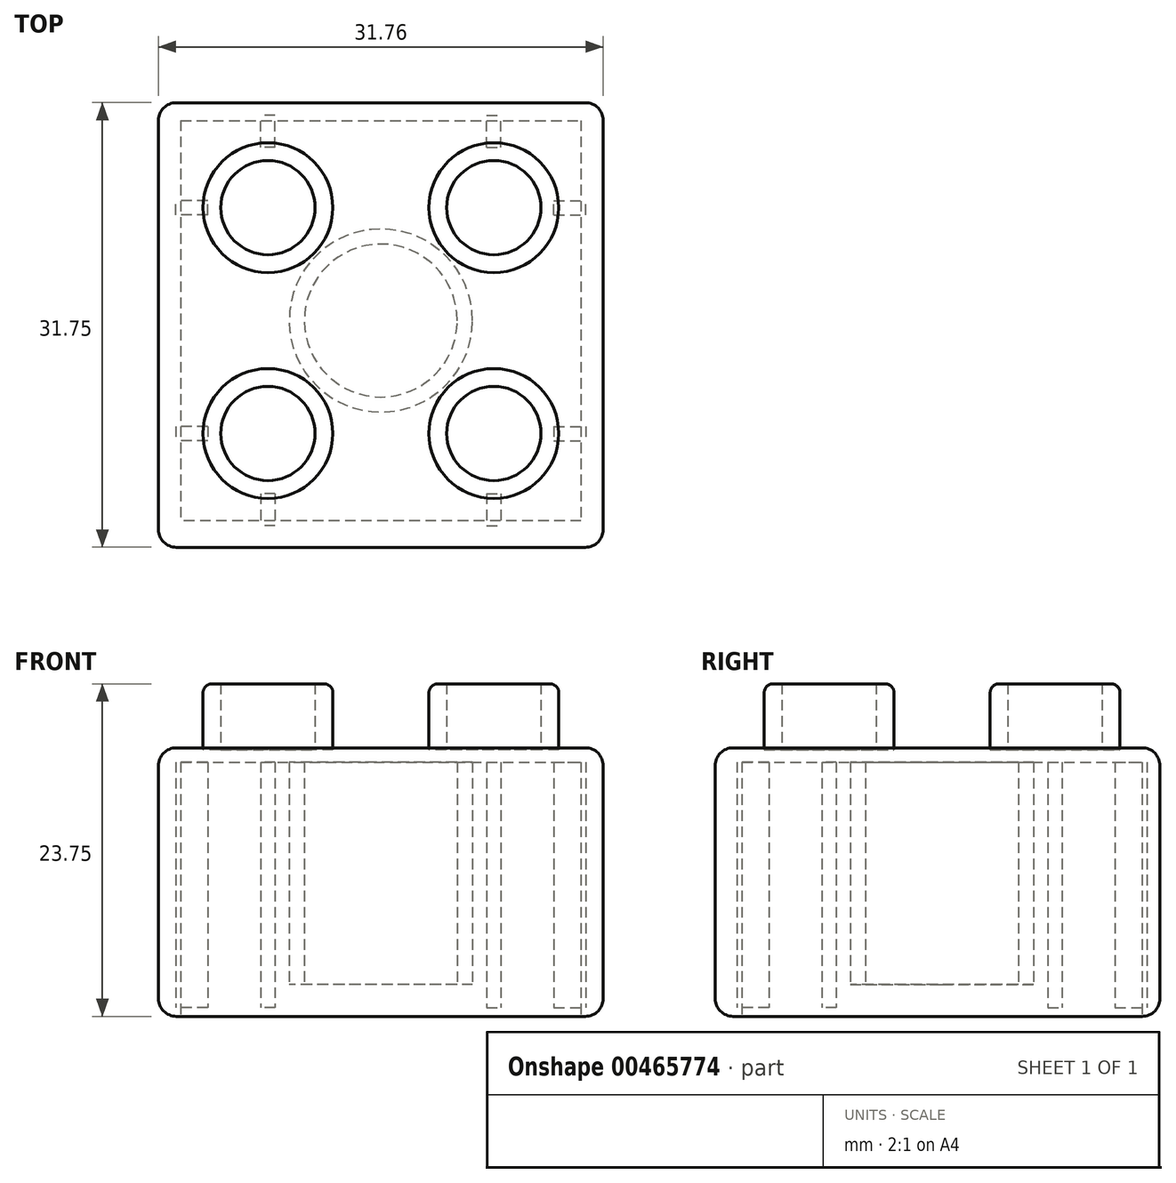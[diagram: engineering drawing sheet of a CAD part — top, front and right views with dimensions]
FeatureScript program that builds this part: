
annotation { "Feature Type Name" : "Feature", "Feature Type Description" : "" }
export const myFeature = defineFeature(function(context is Context, id is Id, definition is map)
    precondition{}
    {
        {
            var Q0;
            Q0=qCreatedBy(makeId("Top.planeOp"),FACE);
            var sketch = newSketch(context, id + "F0", { "sketchPlane" : qUnion([Q0])});
            skPoint(sketch, "E0", {"position": v(0, 16.87) * mm});
            skPoint(sketch, "E1", {"position": v(0, 15.88) * mm});
            skPoint(sketch, "E2", {"position": v(0, -14.88) * mm});
            skPoint(sketch, "E3", {"position": v(0, -15.88) * mm});
            skPoint(sketch, "E4", {"position": v(17.1, 0) * mm});
            skPoint(sketch, "E5", {"position": v(15.88, 0) * mm});
            skPoint(sketch, "E6", {"position": v(-15.88, 0) * mm});
            skPoint(sketch, "E7", {"position": v(15.64, 15.88) * mm});
            skPoint(sketch, "E8", {"position": v(15.88, 15.56) * mm});
            skPoint(sketch, "E9", {"position": v(-16.3, -15.88) * mm});
            skPoint(sketch, "E10", {"position": v(-15.88, -16.2) * mm});
            skLineSegment(sketch, "E11.bottom", {"start": v(-15.88, -16.2) * mm, "end": v(15.88, -16.2) * mm});
            skLineSegment(sketch, "E11.top", {"start": v(-15.88, 15.56) * mm, "end": v(15.88, 15.56) * mm});
            skLineSegment(sketch, "E11.left", {"start": v(-15.88, -16.2) * mm, "end": v(-15.88, 15.56) * mm});
            skLineSegment(sketch, "E11.right", {"start": v(15.88, -16.2) * mm, "end": v(15.88, 15.56) * mm});
            skSolve(sketch);
        }
        {
            var Q0;
            Q0=makeQuery(id+"F0.imprint","IMPRINT",FACE,{"disambiguationData":[TD([[makeQuery(id+"F0.imprint","IMPRINT",EDGE,{"derivedFrom":sQuery(id+"F0.wireOp",EDGE,"E11.bottom")}),1.0]])]});
            var sketch = newSketch(context, id + "F1", { "sketchPlane" : qUnion([Q0])});
            skPoint(sketch, "E12", {"position": v(14.77, 0) * mm});
            skPoint(sketch, "E13", {"position": v(14.29, 0) * mm});
            skPoint(sketch, "E14", {"position": v(-14.29, 0) * mm});
            skPoint(sketch, "E15", {"position": v(-14.29, -14.92) * mm});
            skPoint(sketch, "E16", {"position": v(-14.29, -14.29) * mm});
            skPoint(sketch, "E17", {"position": v(14.29, 14.33) * mm});
            skPoint(sketch, "E18", {"position": v(14.29, 14.29) * mm});
            skLineSegment(sketch, "E19.bottom", {"start": v(-14.29, -14.29) * mm, "end": v(14.29, -14.29) * mm});
            skLineSegment(sketch, "E19.top", {"start": v(-14.29, 14.29) * mm, "end": v(14.29, 14.29) * mm});
            skLineSegment(sketch, "E19.left", {"start": v(-14.29, -14.29) * mm, "end": v(-14.29, 14.29) * mm});
            skLineSegment(sketch, "E19.right", {"start": v(14.29, -14.29) * mm, "end": v(14.29, 14.29) * mm});
            skSolve(sketch);
        }
        {
            var Q0;
            Q0=makeQuery(id+"F1.imprint","IMPRINT",FACE,{"disambiguationData":[TD([[makeQuery(id+"F1.imprint","IMPRINT",EDGE,{"derivedFrom":sQuery(id+"F1.wireOp",EDGE,"E19.bottom")}),1.0]])]});
            var sketch = newSketch(context, id + "F2", { "sketchPlane" : qUnion([Q0])});
            skPoint(sketch, "E20", {"position": v(0, 0) * mm});
            skCircle(sketch, "E21", {"center": v(0, 0) * mm, "radius": 6.54 * mm});
            skSolve(sketch);
        }
        {
            var Q0;
            Q0=makeQuery(id+"F1.imprint","IMPRINT",FACE,{"disambiguationData":[TD([[makeQuery(id+"F1.imprint","IMPRINT",EDGE,{"derivedFrom":sQuery(id+"F1.wireOp",EDGE,"E19.bottom")}),1.0]])]});
            var sketch = newSketch(context, id + "F3", { "sketchPlane" : qUnion([Q0])});
            skPoint(sketch, "E22", {"position": v(0, 0) * mm});
            skCircle(sketch, "E23", {"center": v(0, 0) * mm, "radius": 5.46 * mm});
            skSolve(sketch);
        }
        {
            var Q0;
            Q0=makeQuery(id+"F1.imprint","IMPRINT",FACE,{"disambiguationData":[TD([[makeQuery(id+"F1.imprint","IMPRINT",EDGE,{"derivedFrom":sQuery(id+"F1.wireOp",EDGE,"E19.bottom")}),1.0]])]});
            var sketch = newSketch(context, id + "F4", { "sketchPlane" : qUnion([Q0])});
            skPoint(sketch, "E24", {"position": v(0, 1.02) * mm});
            skPoint(sketch, "E25", {"position": v(0, 0.95) * mm});
            skPoint(sketch, "E26", {"position": v(0, -0.95) * mm});
            skPoint(sketch, "E27", {"position": v(-0.23, 0) * mm});
            skPoint(sketch, "E28", {"position": v(-0.5, 0) * mm});
            skPoint(sketch, "E29", {"position": v(0.3, 0) * mm});
            skPoint(sketch, "E30", {"position": v(0.5, 0) * mm});
            skPoint(sketch, "E31", {"position": v(-0.5, -0.86) * mm});
            skPoint(sketch, "E32", {"position": v(-0.5, -1.5) * mm});
            skPoint(sketch, "E33", {"position": v(0.5, 0.79) * mm});
            skLineSegment(sketch, "E34.bottom", {"start": v(-0.5, -1.5) * mm, "end": v(0.5, -1.5) * mm});
            skLineSegment(sketch, "E34.top", {"start": v(-0.5, 0.79) * mm, "end": v(0.5, 0.79) * mm});
            skLineSegment(sketch, "E34.left", {"start": v(-0.5, -1.5) * mm, "end": v(-0.5, 0.79) * mm});
            skLineSegment(sketch, "E34.right", {"start": v(0.5, -1.5) * mm, "end": v(0.5, 0.79) * mm});
            skPoint(sketch, "E35", {"position": v(14.29, -8.12) * mm});
            skPoint(sketch, "E36", {"position": v(12.29, -8.12) * mm});
            skSolve(sketch);
        }
        {
            var Q0;
            Q0=qSketchRegion(id+"F0",true);
            extrude(context, id + "F5", {"entities" : qUnion([Q0]), "depth" : 19.18 * mm});
        }
        {
            var Q0;
            Q0=qSketchRegion(id+"F1",true);
            extrude(context, id + "F6", {"entities" : qUnion([Q0]), "operationType" : NewBodyOperationType.REMOVE, "depth" : 18.16 * mm, "hasSecondDirection" : true, "secondDirectionOppositeDirection" : true, "secondDirectionDepth" : 0.38 * mm});
        }
        {
            var Q0;
            Q0=qSketchRegion(id+"F2",true);
            extrude(context, id + "F7", {"entities" : qUnion([Q0]), "operationType" : NewBodyOperationType.ADD, "depth" : 15.88 * mm});
        }
        {
            var Q0;
            Q0=qSketchRegion(id+"F3",true);
            extrude(context, id + "F8", {"entities" : qUnion([Q0]), "operationType" : NewBodyOperationType.REMOVE, "depth" : 15.88 * mm, "hasSecondDirection" : true, "secondDirectionOppositeDirection" : true, "secondDirectionDepth" : 0.64 * mm});
        }
        {
            var Q0;
            Q0=makeQuery(id+"F7.opExtrude","SWEPT_BODY",BODY,{"disambiguationData":[OSD([sQuery(id+"F2.wireOp",EDGE,"E21")])]});
            transform(context, id + "F9", {"entities" : qUnion([Q0]), "transformType" : TransformType.TRANSLATION_3D, "dx" : 0 * mm, "dy" : 0 * mm, "dz" : 2.3 * mm, "makeCopy" : false});
        }
        {
            var Q0;
            Q0=makeQuery(id+"F4.imprint","IMPRINT",FACE,{"disambiguationData":[TD([[makeQuery(id+"F4.imprint","IMPRINT",EDGE,{"derivedFrom":sQuery(id+"F4.wireOp",EDGE,"E34.bottom")}),1.0]])]});
            extrude(context, id + "F10", {"entities" : qUnion([Q0]), "operationType" : NewBodyOperationType.ADD, "depth" : 17.53 * mm});
        }
        {
            var Q0;
            Q0=makeQuery(id+"F10.opExtrude","SWEPT_BODY",BODY,{"disambiguationData":[OSD([sQuery(id+"F4.wireOp",EDGE,"E34.bottom"),sQuery(id+"F4.wireOp",EDGE,"E34.top"),sQuery(id+"F4.wireOp",EDGE,"E34.left"),sQuery(id+"F4.wireOp",EDGE,"E34.right")])]});
            transform(context, id + "F11", {"entities" : qUnion([Q0]), "transformType" : TransformType.TRANSLATION_3D, "dx" : 8.06 * mm, "dy" : 13.86 * mm, "dz" : 0.64 * mm, "makeCopy" : false});
        }
        {
            var Q0;
            Q0=makeQuery(id+"F10.opExtrude","SWEPT_BODY",BODY,{"disambiguationData":[OSD([sQuery(id+"F4.wireOp",EDGE,"E34.bottom"),sQuery(id+"F4.wireOp",EDGE,"E34.top"),sQuery(id+"F4.wireOp",EDGE,"E34.left"),sQuery(id+"F4.wireOp",EDGE,"E34.right")])]});
            var Q1;
            Q1=qCreatedBy(makeId("Front.planeOp"),FACE);
            mirror(context, id + "F12", {"entities" : qUnion([Q0]), "mirrorPlane" : qUnion([Q1])});
        }
        {
            var Q0;
            Q0=makeQuery(id+"F12.opPattern","COPY",BODY,{"derivedFrom":makeQuery(id+"F10.opExtrude","SWEPT_BODY",BODY,{"disambiguationData":[OSD([sQuery(id+"F4.wireOp",EDGE,"E34.bottom"),sQuery(id+"F4.wireOp",EDGE,"E34.top"),sQuery(id+"F4.wireOp",EDGE,"E34.left"),sQuery(id+"F4.wireOp",EDGE,"E34.right")])]}),"instanceName":"1"});
            var Q1;
            Q1=makeQuery(id+"F10.opExtrude","SWEPT_BODY",BODY,{"disambiguationData":[OSD([sQuery(id+"F4.wireOp",EDGE,"E34.bottom"),sQuery(id+"F4.wireOp",EDGE,"E34.top"),sQuery(id+"F4.wireOp",EDGE,"E34.left"),sQuery(id+"F4.wireOp",EDGE,"E34.right")])]});
            var Q2;
            Q2=qCreatedBy(makeId("Right.planeOp"),FACE);
            mirror(context, id + "F13", {"entities" : qUnion([Q0, Q1]), "mirrorPlane" : qUnion([Q2])});
        }
        {
            var Q0;
            Q0=qCreatedBy(makeId("Front.planeOp"),FACE);
            var sketch = newSketch(context, id + "F14", { "sketchPlane" : qUnion([Q0])});
            skLineSegment(sketch, "E37", {"start": v(0, 40.9) * mm, "end": v(0, -32.36) * mm});
            skSolve(sketch);
        }
        {
            var Q0;
            Q0=makeQuery(id+"F12.opPattern","COPY",BODY,{"derivedFrom":makeQuery(id+"F10.opExtrude","SWEPT_BODY",BODY,{"disambiguationData":[OSD([sQuery(id+"F4.wireOp",EDGE,"E34.bottom"),sQuery(id+"F4.wireOp",EDGE,"E34.top"),sQuery(id+"F4.wireOp",EDGE,"E34.left"),sQuery(id+"F4.wireOp",EDGE,"E34.right")])]}),"instanceName":"1"});
            var Q1;
            Q1=makeQuery(id+"F13.opPattern","COPY",BODY,{"derivedFrom":makeQuery(id+"F12.opPattern","COPY",BODY,{"derivedFrom":makeQuery(id+"F10.opExtrude","SWEPT_BODY",BODY,{"disambiguationData":[OSD([sQuery(id+"F4.wireOp",EDGE,"E34.bottom"),sQuery(id+"F4.wireOp",EDGE,"E34.top"),sQuery(id+"F4.wireOp",EDGE,"E34.left"),sQuery(id+"F4.wireOp",EDGE,"E34.right")])]}),"instanceName":"1"}),"instanceName":"1"});
            var Q2;
            Q2=makeQuery(id+"F10.opExtrude","SWEPT_BODY",BODY,{"disambiguationData":[OSD([sQuery(id+"F4.wireOp",EDGE,"E34.bottom"),sQuery(id+"F4.wireOp",EDGE,"E34.top"),sQuery(id+"F4.wireOp",EDGE,"E34.left"),sQuery(id+"F4.wireOp",EDGE,"E34.right")])]});
            var Q3;
            Q3=makeQuery(id+"F13.opPattern","COPY",BODY,{"derivedFrom":makeQuery(id+"F10.opExtrude","SWEPT_BODY",BODY,{"disambiguationData":[OSD([sQuery(id+"F4.wireOp",EDGE,"E34.bottom"),sQuery(id+"F4.wireOp",EDGE,"E34.top"),sQuery(id+"F4.wireOp",EDGE,"E34.left"),sQuery(id+"F4.wireOp",EDGE,"E34.right")])]}),"instanceName":"1"});
            var Q4;
            Q4=sQuery(id+"F14.wireOp",EDGE,"E37");
            transform(context, id + "F15", {"entities" : qUnion([Q0, Q1, Q2, Q3]), "transformType" : TransformType.ROTATION, "transformAxis" : qUnion([Q4]), "angle" : 90 * degree, "makeCopy" : true});
        }
        {
            var Q0;
            Q0=qCreatedBy(makeId("Top.planeOp"),FACE);
            var sketch = newSketch(context, id + "F16", { "sketchPlane" : qUnion([Q0])});
            skCircle(sketch, "E38", {"center": v(0, 0) * mm, "radius": 4.64 * mm});
            skSolve(sketch);
        }
        {
            var Q0;
            Q0=qCreatedBy(makeId("Top.planeOp"),FACE);
            var sketch = newSketch(context, id + "F17", { "sketchPlane" : qUnion([Q0])});
            skCircle(sketch, "E39", {"center": v(0, 0) * mm, "radius": 3.37 * mm});
            skSolve(sketch);
        }
        {
            var Q0;
            Q0=makeQuery(id+"F16.imprint","IMPRINT",FACE,{"disambiguationData":[TD([[makeQuery(id+"F16.imprint","IMPRINT",EDGE,{"derivedFrom":sQuery(id+"F16.wireOp",EDGE,"E38")}),1.0]])]});
            extrude(context, id + "F18", {"entities" : qUnion([Q0]), "depth" : 4.7 * mm});
        }
        {
            var Q0;
            Q0=makeQuery(id+"F17.imprint","IMPRINT",FACE,{"disambiguationData":[TD([[makeQuery(id+"F17.imprint","IMPRINT",EDGE,{"derivedFrom":sQuery(id+"F17.wireOp",EDGE,"E39")}),1.0]])]});
            extrude(context, id + "F19", {"entities" : qUnion([Q0]), "operationType" : NewBodyOperationType.REMOVE, "depth" : 4.7 * mm});
        }
        {
            var Q0;
            Q0=makeQuery(id+"F18.opExtrude","SWEPT_BODY",BODY,{"disambiguationData":[OSD([sQuery(id+"F16.wireOp",EDGE,"E38")])]});
            transform(context, id + "F20", {"entities" : qUnion([Q0]), "transformType" : TransformType.TRANSLATION_3D, "dx" : 8.06 * mm, "dy" : 8.06 * mm, "dz" : 19.05 * mm, "makeCopy" : false});
        }
        {
            var Q0;
            Q0=makeQuery(id+"F18.opExtrude","SWEPT_BODY",BODY,{"disambiguationData":[OSD([sQuery(id+"F16.wireOp",EDGE,"E38")])]});
            var Q1;
            Q1=qCreatedBy(makeId("Front.planeOp"),FACE);
            mirror(context, id + "F21", {"entities" : qUnion([Q0]), "mirrorPlane" : qUnion([Q1])});
        }
        {
            var Q0;
            Q0=makeQuery(id+"F18.opExtrude","SWEPT_BODY",BODY,{"disambiguationData":[OSD([sQuery(id+"F16.wireOp",EDGE,"E38")])]});
            var Q1;
            Q1=makeQuery(id+"F21.opPattern","COPY",BODY,{"derivedFrom":makeQuery(id+"F18.opExtrude","SWEPT_BODY",BODY,{"disambiguationData":[OSD([sQuery(id+"F16.wireOp",EDGE,"E38")])]}),"instanceName":"1"});
            var Q2;
            Q2=qCreatedBy(makeId("Right.planeOp"),FACE);
            mirror(context, id + "F22", {"entities" : qUnion([Q0, Q1]), "mirrorPlane" : qUnion([Q2])});
        }
        {
            var Q0;
            Q0=makeQuery(id+"F5.opExtrude","CAP_EDGE",EDGE,{"disambiguationData":[OSD([sQuery(id+"F0.wireOp",EDGE,"E11.bottom")])],"isStart":false});
            var Q1;
            Q1=makeQuery(id+"F5.opExtrude","CAP_EDGE",EDGE,{"disambiguationData":[OSD([sQuery(id+"F0.wireOp",EDGE,"E11.left")])],"isStart":false});
            var Q2;
            Q2=makeQuery(id+"F5.opExtrude","CAP_EDGE",EDGE,{"disambiguationData":[OSD([sQuery(id+"F0.wireOp",EDGE,"E11.top")])],"isStart":false});
            var Q3;
            Q3=makeQuery(id+"F5.opExtrude","CAP_EDGE",EDGE,{"disambiguationData":[OSD([sQuery(id+"F0.wireOp",EDGE,"E11.right")])],"isStart":false});
            var Q4;
            Q4=makeQuery(id+"F5.opExtrude","SWEPT_EDGE",EDGE,{"disambiguationData":[OSD([sQuery(id+"F0.wireOp",EDGE,"E11.bottom"),sQuery(id+"F0.wireOp",EDGE,"E11.left")])]});
            var Q5;
            Q5=makeQuery(id+"F5.opExtrude","SWEPT_EDGE",EDGE,{"disambiguationData":[OSD([sQuery(id+"F0.wireOp",EDGE,"E11.bottom"),sQuery(id+"F0.wireOp",EDGE,"E11.right")])]});
            var Q6;
            Q6=makeQuery(id+"F5.opExtrude","SWEPT_EDGE",EDGE,{"disambiguationData":[OSD([sQuery(id+"F0.wireOp",EDGE,"E11.top"),sQuery(id+"F0.wireOp",EDGE,"E11.left")])]});
            var Q7;
            Q7=makeQuery(id+"F5.opExtrude","SWEPT_EDGE",EDGE,{"disambiguationData":[OSD([sQuery(id+"F0.wireOp",EDGE,"E11.top"),sQuery(id+"F0.wireOp",EDGE,"E11.right")])]});
            var Q8;
            Q8=makeQuery(id+"F5.opExtrude","CAP_EDGE",EDGE,{"disambiguationData":[OSD([sQuery(id+"F0.wireOp",EDGE,"E11.right")])],"isStart":true});
            var Q9;
            Q9=makeQuery(id+"F5.opExtrude","CAP_EDGE",EDGE,{"disambiguationData":[OSD([sQuery(id+"F0.wireOp",EDGE,"E11.bottom")])],"isStart":true});
            var Q10;
            Q10=makeQuery(id+"F5.opExtrude","CAP_EDGE",EDGE,{"disambiguationData":[OSD([sQuery(id+"F0.wireOp",EDGE,"E11.left")])],"isStart":true});
            var Q11;
            Q11=makeQuery(id+"F5.opExtrude","CAP_EDGE",EDGE,{"disambiguationData":[OSD([sQuery(id+"F0.wireOp",EDGE,"E11.top")])],"isStart":true});
            fillet(context, id + "F23", {"entities" : qUnion([Q0, Q1, Q2, Q3, Q4, Q5, Q6, Q7, Q8, Q9, Q10, Q11]), "radius" : 1.27 * mm, "tangentPropagation" : true, "allowEdgeOverflow" : false});
        }
        {
            var Q0;
            Q0=makeQuery(id+"F22.opPattern","COPY",EDGE,{"derivedFrom":makeQuery(id+"F18.opExtrude","CAP_EDGE",EDGE,{"disambiguationData":[OSD([sQuery(id+"F16.wireOp",EDGE,"E38")])],"isStart":false}),"instanceName":"1"});
            var Q1;
            Q1=makeQuery(id+"F18.opExtrude","CAP_EDGE",EDGE,{"disambiguationData":[OSD([sQuery(id+"F16.wireOp",EDGE,"E38")])],"isStart":false});
            var Q2;
            Q2=makeQuery(id+"F21.opPattern","COPY",EDGE,{"derivedFrom":makeQuery(id+"F18.opExtrude","CAP_EDGE",EDGE,{"disambiguationData":[OSD([sQuery(id+"F16.wireOp",EDGE,"E38")])],"isStart":false}),"instanceName":"1"});
            var Q3;
            Q3=makeQuery(id+"F22.opPattern","COPY",EDGE,{"derivedFrom":makeQuery(id+"F21.opPattern","COPY",EDGE,{"derivedFrom":makeQuery(id+"F18.opExtrude","CAP_EDGE",EDGE,{"disambiguationData":[OSD([sQuery(id+"F16.wireOp",EDGE,"E38")])],"isStart":false}),"instanceName":"1"}),"instanceName":"1"});
            fillet(context, id + "F24", {"entities" : qUnion([Q0, Q1, Q2, Q3]), "radius" : 0.64 * mm, "tangentPropagation" : true, "allowEdgeOverflow" : false});
        }
    });
